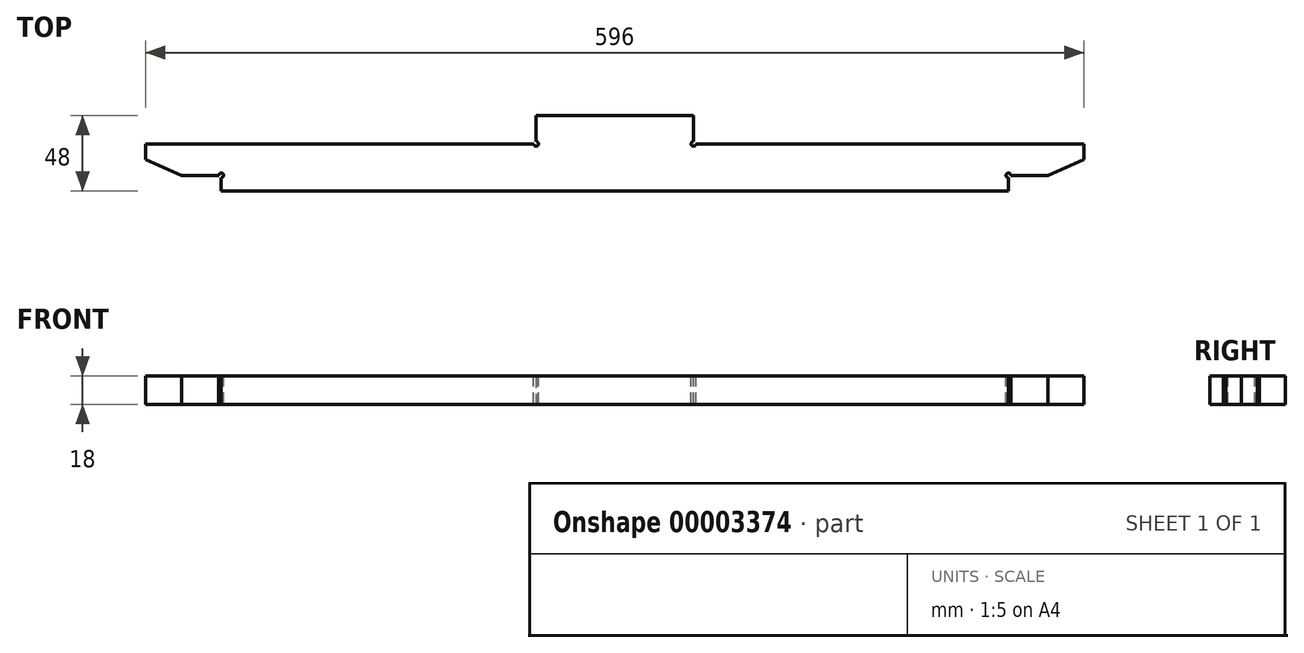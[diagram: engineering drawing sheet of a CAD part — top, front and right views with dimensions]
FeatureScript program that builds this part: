
annotation { "Feature Type Name" : "Feature", "Feature Type Description" : "" }
export const myFeature = defineFeature(function(context is Context, id is Id, definition is map)
    precondition{}
    {
        {
            var Q0;
            Q0=qCreatedBy(makeId("Top.planeOp"),FACE);
            var sketch = newSketch(context, id + "F0", { "sketchPlane" : qUnion([Q0])});
            skLineSegment(sketch, "E0", {"start": v(-203.66, 20) * mm, "end": v(44.34, 20) * mm});
            skLineSegment(sketch, "E1", {"start": v(0, -10) * mm, "end": v(-155.66, -10) * mm});
            skLineSegment(sketch, "E2", {"start": v(-155.66, -10) * mm, "end": v(-155.66, 0) * mm});
            skLineSegment(sketch, "E3", {"start": v(-155.66, 0) * mm, "end": v(-180.66, 0) * mm});
            skLineSegment(sketch, "E4", {"start": v(-203.66, 10) * mm, "end": v(-203.66, 20) * mm});
            skLineSegment(sketch, "E5", {"start": v(-203.66, 10) * mm, "end": v(-180.66, 0) * mm});
            skLineSegment(sketch, "E6.1.MirrorCS", {"start": v(392.34, 20) * mm, "end": v(144.34, 20) * mm});
            skLineSegment(sketch, "E6.2.MirrorCS", {"start": v(0, -10) * mm, "end": v(344.34, -10) * mm});
            skLineSegment(sketch, "E6.4.MirrorCS", {"start": v(392.34, 10) * mm, "end": v(369.34, 0) * mm});
            skLineSegment(sketch, "E6.5.MirrorCS", {"start": v(344.34, -10) * mm, "end": v(344.34, 0) * mm});
            skLineSegment(sketch, "E6.6.MirrorCS", {"start": v(392.34, 10) * mm, "end": v(392.34, 20) * mm});
            skLineSegment(sketch, "E6.7.MirrorCS", {"start": v(344.34, 0) * mm, "end": v(369.34, 0) * mm});
            skLineSegment(sketch, "E7.rect.bottom", {"start": v(44.34, 38) * mm, "end": v(144.34, 38) * mm});
            skLineSegment(sketch, "E7.rect.left", {"start": v(44.34, 38) * mm, "end": v(44.34, 20) * mm});
            skLineSegment(sketch, "E7.rect.right", {"start": v(144.34, 38) * mm, "end": v(144.34, 20) * mm});
            skSolve(sketch);
        }
        {
            var Q0;
            Q0=makeQuery(id+"F0.imprint","IMPRINT",FACE,{"disambiguationData":[TD([[makeQuery(id+"F0.imprint","IMPRINT",EDGE,{"derivedFrom":sQuery(id+"F0.wireOp",EDGE,"E0")}),-1.0]])]});
            extrude(context, id + "F1", {"entities" : qUnion([Q0]), "depth" : 18 * mm});
        }
        {
            var Q0;
            Q0=makeQuery(id+"F1.opExtrude","CAP_FACE",FACE,{"disambiguationData":[OSD([sQuery(id+"F0.wireOp",EDGE,"E0"),sQuery(id+"F0.wireOp",EDGE,"E1"),sQuery(id+"F0.wireOp",EDGE,"E2"),sQuery(id+"F0.wireOp",EDGE,"E3"),sQuery(id+"F0.wireOp",EDGE,"E4"),sQuery(id+"F0.wireOp",EDGE,"E5"),sQuery(id+"F0.wireOp",EDGE,"E6.1.MirrorCS"),sQuery(id+"F0.wireOp",EDGE,"E6.4.MirrorCS"),sQuery(id+"F0.wireOp",EDGE,"E6.5.MirrorCS"),sQuery(id+"F0.wireOp",EDGE,"E6.6.MirrorCS"),sQuery(id+"F0.wireOp",EDGE,"E6.7.MirrorCS"),sQuery(id+"F0.wireOp",EDGE,"E7.rect.bottom"),sQuery(id+"F0.wireOp",EDGE,"E7.rect.left"),sQuery(id+"F0.wireOp",EDGE,"E7.rect.right")])],"isStart":false});
            var sketch = newSketch(context, id + "F2", { "sketchPlane" : qUnion([Q0])});
            skCircle(sketch, "E8", {"center": v(-155.66, 0) * mm, "radius": 1.5 * mm});
            skCircle(sketch, "E9", {"center": v(144.34, 20) * mm, "radius": 1.5 * mm});
            skCircle(sketch, "E10", {"center": v(44.34, 20) * mm, "radius": 1.5 * mm});
            skCircle(sketch, "E11", {"center": v(344.34, 0) * mm, "radius": 1.5 * mm});
            skSolve(sketch);
        }
        {
            var Q0;
            {var subQ1=sQuery(id+"F2.wireOp",EDGE,"E8");var subQ3=makeQuery(id+"F1.opExtrude","CAP_EDGE",EDGE,{"disambiguationData":[OSD([sQuery(id+"F0.wireOp",EDGE,"E2")])],"isStart":false});var subQ6=makeQuery(id+"F2.imprint","INTERSECT",VERTEX,{"derivedFrom":[subQ3,subQ1]});var subQ9=sQuery(id+"F2.wireOp",EDGE,"E9");var subQ11=makeQuery(id+"F1.opExtrude","CAP_EDGE",EDGE,{"disambiguationData":[OSD([sQuery(id+"F0.wireOp",EDGE,"E6.1.MirrorCS")])],"isStart":false});var subQ14=makeQuery(id+"F2.imprint","INTERSECT",VERTEX,{"derivedFrom":[subQ11,subQ9]});var subQ17=sQuery(id+"F2.wireOp",EDGE,"E10");var subQ19=makeQuery(id+"F1.opExtrude","CAP_EDGE",EDGE,{"disambiguationData":[OSD([sQuery(id+"F0.wireOp",EDGE,"E0")])],"isStart":false});var subQ22=makeQuery(id+"F2.imprint","INTERSECT",VERTEX,{"derivedFrom":[subQ19,subQ17]});var subQ25=sQuery(id+"F2.wireOp",EDGE,"E11");var subQ27=makeQuery(id+"F1.opExtrude","CAP_EDGE",EDGE,{"disambiguationData":[OSD([sQuery(id+"F0.wireOp",EDGE,"E6.5.MirrorCS")])],"isStart":false});var subQ30=makeQuery(id+"F2.imprint","INTERSECT",VERTEX,{"derivedFrom":[subQ27,subQ25]});Q0=qUnion([makeQuery(id+"F2.imprint","IMPRINT",FACE,{"disambiguationData":[TD([[makeQuery(id+"F2.imprint","IMPRINT",EDGE,{"disambiguationData":[TD([[subQ6,1.0]])],"derivedFrom":subQ1}),1.0]])]}),makeQuery(id+"F2.imprint","IMPRINT",FACE,{"disambiguationData":[TD([[makeQuery(id+"F2.imprint","IMPRINT",EDGE,{"disambiguationData":[TD([[subQ14,-1.0]])],"derivedFrom":subQ9}),1.0]])]}),makeQuery(id+"F2.imprint","IMPRINT",FACE,{"disambiguationData":[TD([[makeQuery(id+"F2.imprint","IMPRINT",EDGE,{"disambiguationData":[TD([[subQ22,1.0]])],"derivedFrom":subQ17}),1.0]])]}),makeQuery(id+"F2.imprint","IMPRINT",FACE,{"disambiguationData":[TD([[makeQuery(id+"F2.imprint","IMPRINT",EDGE,{"disambiguationData":[TD([[subQ30,-1.0]])],"derivedFrom":subQ25}),1.0]])]}),makeQuery(id+"F2.imprint","IMPRINT",FACE,{"disambiguationData":[TD([[makeQuery(id+"F2.imprint","IMPRINT",EDGE,{"disambiguationData":[TD([[subQ6,-1.0]])],"derivedFrom":subQ1}),1.0]])]}),makeQuery(id+"F2.imprint","IMPRINT",FACE,{"disambiguationData":[TD([[makeQuery(id+"F2.imprint","IMPRINT",EDGE,{"disambiguationData":[TD([[subQ14,1.0]])],"derivedFrom":subQ9}),1.0]])]}),makeQuery(id+"F2.imprint","IMPRINT",FACE,{"disambiguationData":[TD([[makeQuery(id+"F2.imprint","IMPRINT",EDGE,{"disambiguationData":[TD([[subQ22,-1.0]])],"derivedFrom":subQ17}),1.0]])]}),makeQuery(id+"F2.imprint","IMPRINT",FACE,{"disambiguationData":[TD([[makeQuery(id+"F2.imprint","IMPRINT",EDGE,{"disambiguationData":[TD([[subQ30,1.0]])],"derivedFrom":subQ25}),1.0]])]})]);}
            extrude(context, id + "F3", {"entities" : qUnion([Q0]), "operationType" : NewBodyOperationType.REMOVE, "oppositeDirection" : true, "depth" : 25 * mm});
        }
    });
